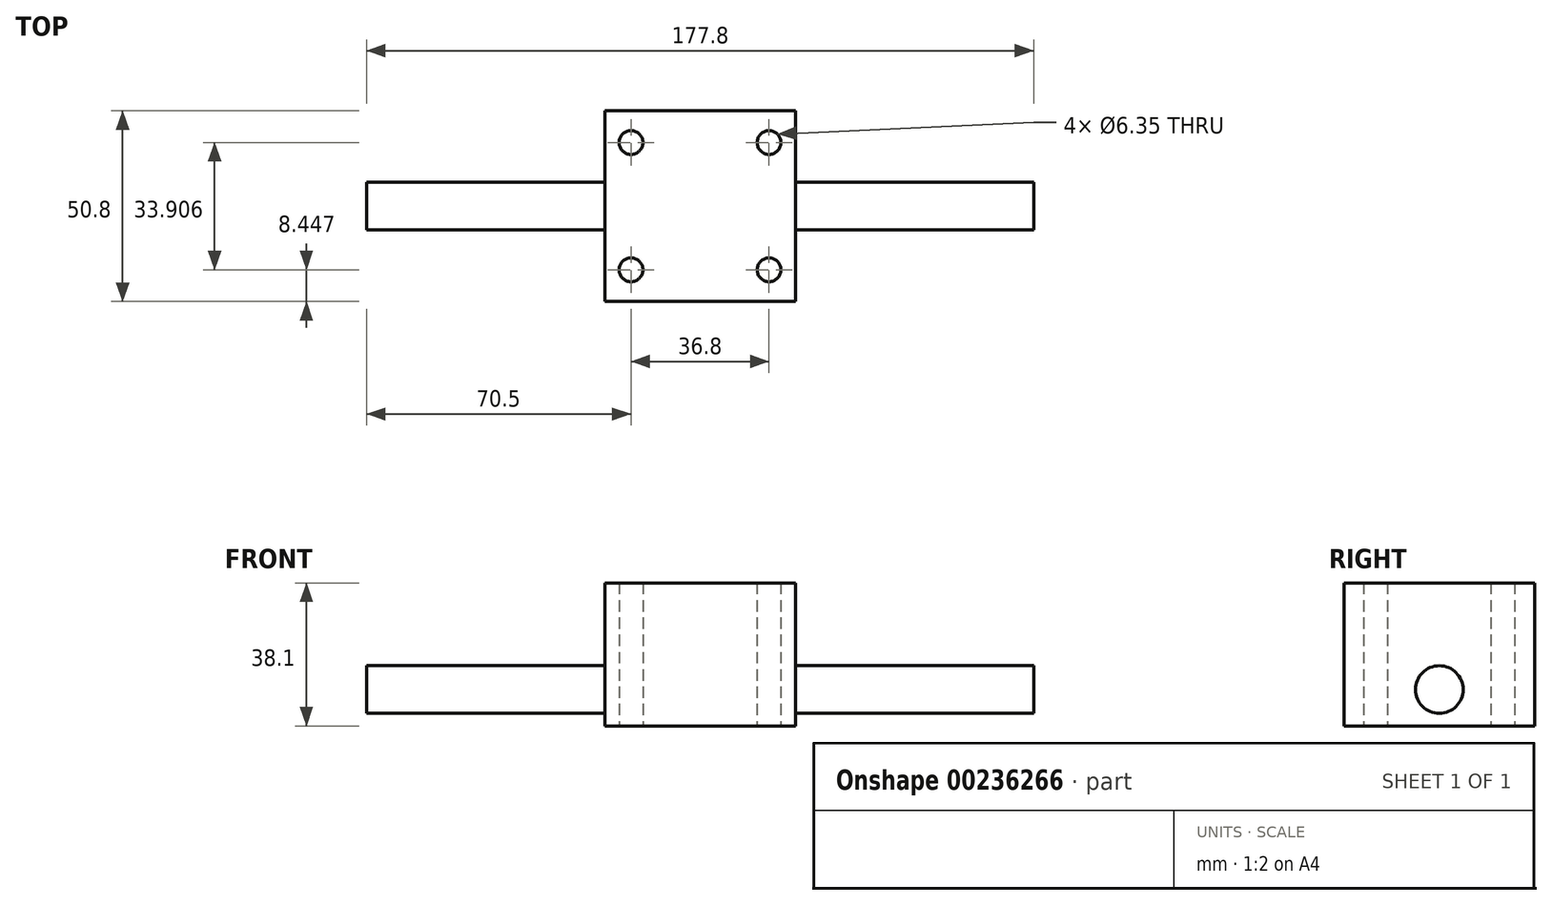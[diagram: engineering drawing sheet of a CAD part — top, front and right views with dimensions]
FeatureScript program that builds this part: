
annotation { "Feature Type Name" : "Feature", "Feature Type Description" : "" }
export const myFeature = defineFeature(function(context is Context, id is Id, definition is map)
    precondition{}
    {
        {
            var Q0;
            Q0=qCreatedBy(makeId("Top.planeOp"),FACE);
            var sketch = newSketch(context, id + "F0", { "sketchPlane" : qUnion([Q0])});
            skLineSegment(sketch, "E0.bottom", {"start": v(-25.4, 25.4) * mm, "end": v(25.4, 25.4) * mm});
            skLineSegment(sketch, "E0.top", {"start": v(-25.4, -25.4) * mm, "end": v(25.4, -25.4) * mm});
            skLineSegment(sketch, "E0.left", {"start": v(-25.4, 25.4) * mm, "end": v(-25.4, -25.4) * mm});
            skLineSegment(sketch, "E0.right", {"start": v(25.4, 25.4) * mm, "end": v(25.4, -25.4) * mm});
            skPoint(sketch, "E0.middle", {"position": v(0, 0) * mm});
            skCircle(sketch, "E1", {"center": v(-18.4, 16.95) * mm, "radius": 3.18 * mm});
            skCircle(sketch, "E2.MirrorC", {"center": v(18.4, 16.95) * mm, "radius": 3.18 * mm});
            skCircle(sketch, "E3.MirrorC", {"center": v(-18.4, -16.95) * mm, "radius": 3.18 * mm});
            skCircle(sketch, "E4.MirrorC", {"center": v(18.4, -16.95) * mm, "radius": 3.18 * mm});
            skSolve(sketch);
        }
        {
            var Q0;
            Q0 = qSketchRegion(id + "F0", true);
            extrude(context, id + "F1", {"entities" : qUnion([Q0]), "endBound" : BoundingType.SYMMETRIC, "depth" : 38.1 * mm});
        }
        {
            var Q0;
            Q0=makeQuery(id+"F1.opExtrude","SWEPT_FACE",FACE,{"disambiguationData":[OSD([sQuery(id+"F0.wireOp",EDGE,"E0.left")])]});
            var sketch = newSketch(context, id + "F2", { "sketchPlane" : qUnion([Q0])});
            skCircle(sketch, "E5", {"center": v(0, -9.35) * mm, "radius": 6.35 * mm});
            skSolve(sketch);
        }
        {
            var Q0;
            Q0 = qSketchRegion(id + "F2", true);
            extrude(context, id + "F3", {"entities" : qUnion([Q0]), "operationType" : NewBodyOperationType.ADD, "depth" : 63.5 * mm});
        }
        {
            var Q0;
            Q0=makeQuery(id+"F1.opExtrude","SWEPT_BODY",BODY,{"disambiguationData":[OSD([sQuery(id+"F0.wireOp",EDGE,"E0.bottom"),sQuery(id+"F0.wireOp",EDGE,"E0.top"),sQuery(id+"F0.wireOp",EDGE,"E0.left"),sQuery(id+"F0.wireOp",EDGE,"E0.right"),sQuery(id+"F0.wireOp",EDGE,"E1"),sQuery(id+"F0.wireOp",EDGE,"E2.MirrorC"),sQuery(id+"F0.wireOp",EDGE,"E3.MirrorC"),sQuery(id+"F0.wireOp",EDGE,"E4.MirrorC")])]});
            var Q1;
            Q1=qCreatedBy(makeId("Right.planeOp"),FACE);
            mirror(context, id + "F4", {"operationType" : NewBodyOperationType.ADD, "entities" : qUnion([Q0]), "mirrorPlane" : qUnion([Q1])});
        }
    });
